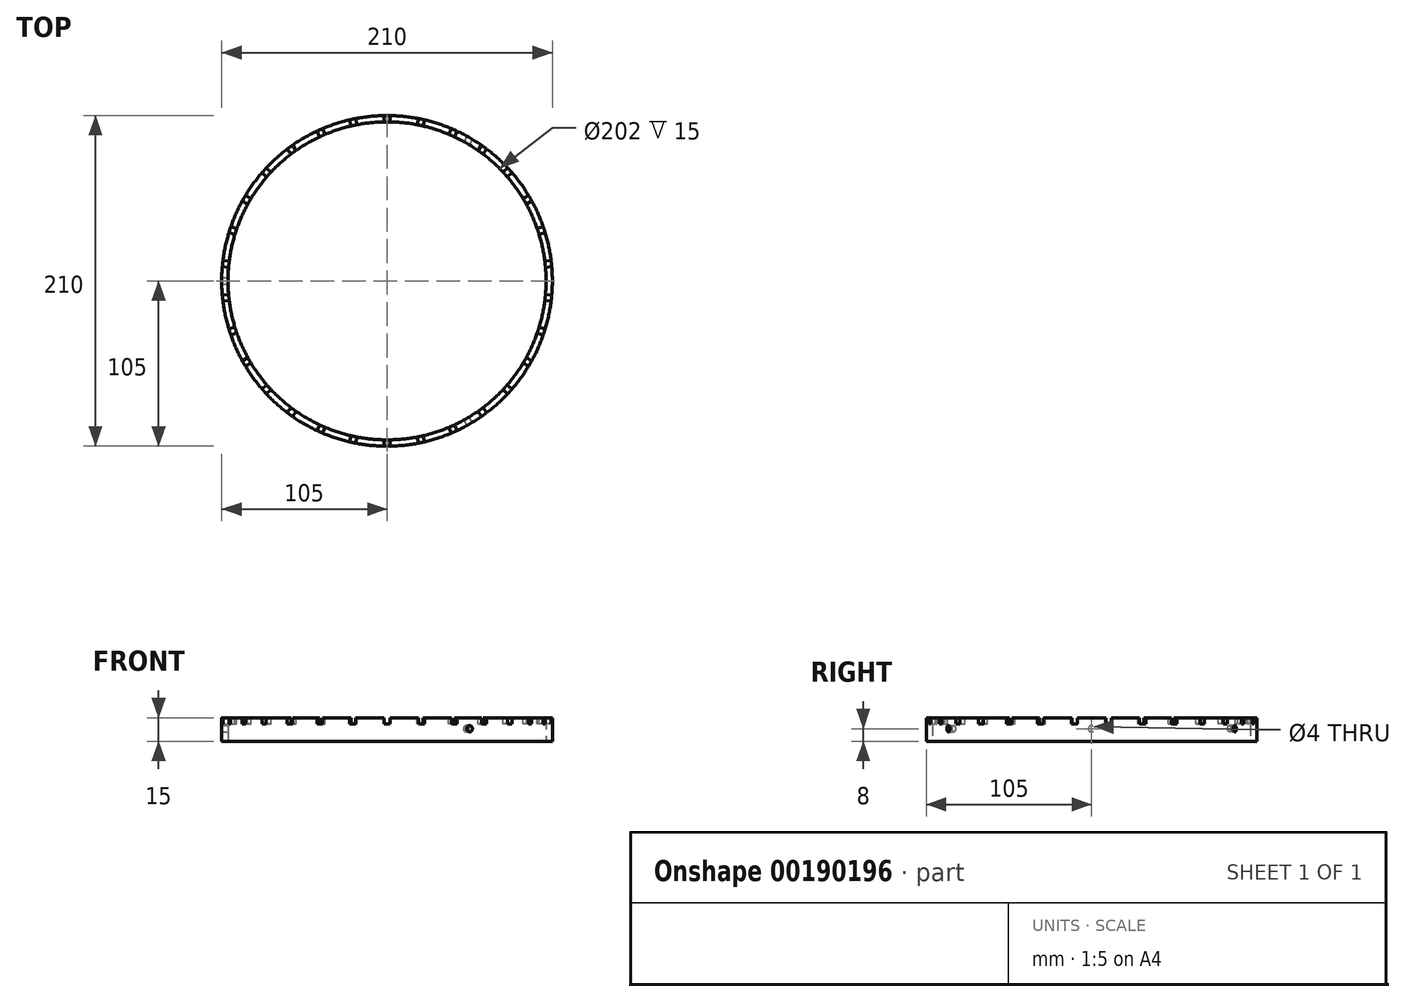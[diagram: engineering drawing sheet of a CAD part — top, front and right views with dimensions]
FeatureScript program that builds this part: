
annotation { "Feature Type Name" : "Feature", "Feature Type Description" : "" }
export const myFeature = defineFeature(function(context is Context, id is Id, definition is map)
    precondition{}
    {
        {
            var Q0;
            Q0=qCreatedBy(makeId("Top.planeOp"),FACE);
            var sketch = newSketch(context, id + "F0", { "sketchPlane" : qUnion([Q0])});
            skCircle(sketch, "E0", {"center": v(0, 0) * mm, "radius": 105 * mm});
            skCircle(sketch, "E1", {"center": v(0, 0) * mm, "radius": 101 * mm});
            skSolve(sketch);
        }
        {
            var Q0;
            Q0=makeQuery(id+"F0.imprint","IMPRINT",FACE,{"disambiguationData":[TD([[makeQuery(id+"F0.imprint","IMPRINT",EDGE,{"derivedFrom":sQuery(id+"F0.wireOp",EDGE,"E0")}),1.0]])]});
            extrude(context, id + "F1", {"entities" : qUnion([Q0]), "depth" : 15 * mm});
        }
        {
            var Q0;
            Q0=makeQuery(id+"F1.opExtrude","CAP_FACE",FACE,{"disambiguationData":[OSD([sQuery(id+"F0.wireOp",EDGE,"E0"),sQuery(id+"F0.wireOp",EDGE,"E1")])],"isStart":false});
            var sketch = newSketch(context, id + "F2", { "sketchPlane" : qUnion([Q0])});
            skLineSegment(sketch, "E2.bottom", {"start": v(2, 107.5) * mm, "end": v(-2, 107.5) * mm});
            skLineSegment(sketch, "E2.top", {"start": v(2, 97.86) * mm, "end": v(-2, 97.86) * mm});
            skLineSegment(sketch, "E2.left", {"start": v(2, 107.5) * mm, "end": v(2, 97.86) * mm});
            skLineSegment(sketch, "E2.right", {"start": v(-2, 107.5) * mm, "end": v(-2, 97.86) * mm});
            skPoint(sketch, "E2.middle", {"position": v(0, 102.68) * mm});
            skSolve(sketch);
        }
        {
            var Q0;
            {var subQ0=sQuery(id+"F2.wireOp",EDGE,"E2.left");var subQ1=makeQuery(id+"F1.opExtrude","CAP_EDGE",EDGE,{"disambiguationData":[OSD([sQuery(id+"F0.wireOp",EDGE,"E0")])],"isStart":false});var subQ2=makeQuery(id+"F2.imprint","INTERSECT",VERTEX,{"derivedFrom":[subQ1,subQ0]});Q0=makeQuery(id+"F2.imprint","IMPRINT",FACE,{"disambiguationData":[TD([[makeQuery(id+"F2.imprint","IMPRINT",EDGE,{"disambiguationData":[TD([[subQ2,-1.0]])],"derivedFrom":subQ0}),-1.0]])]});}
            extrude(context, id + "F3", {"entities" : qUnion([Q0]), "oppositeDirection" : true, "depth" : 4 * mm});
        }
        {
            var Q0;
            Q0=qCreatedBy(makeId("Right.planeOp"),FACE);
            var sketch = newSketch(context, id + "F4", { "sketchPlane" : qUnion([Q0])});
            skLineSegment(sketch, "E3", {"start": v(0, 0) * mm, "end": v(0, 34.11) * mm});
            skSolve(sketch);
        }
        {
            var Q0;
            Q0=makeQuery(id+"F3.opExtrude","SWEPT_BODY",BODY,{"disambiguationData":[OSD([sQuery(id+"F0.wireOp",EDGE,"E0"),sQuery(id+"F0.wireOp",EDGE,"E1"),sQuery(id+"F2.wireOp",EDGE,"E2.left"),sQuery(id+"F2.wireOp",EDGE,"E2.right")])]});
            var Q1;
            Q1=sQuery(id+"F4.wireOp",EDGE,"E3");
            circularPattern(context, id + "F5", {"entities" : qUnion([Q0]), "axis" : qUnion([Q1]), "angle" : 360 * degree, "instanceCount" : 30, "equalSpace" : true});
        }
        {
            var Q0;
            Q0=qCreatedBy(makeId("Right.planeOp"),FACE);
            var sketch = newSketch(context, id + "F6", { "sketchPlane" : qUnion([Q0])});
            skCircle(sketch, "E4", {"center": v(0, 8) * mm, "radius": 2 * mm});
            skSolve(sketch);
        }
        {
            var Q0;
            Q0=makeQuery(id+"F6.imprint","IMPRINT",FACE,{"disambiguationData":[TD([[makeQuery(id+"F6.imprint","IMPRINT",EDGE,{"derivedFrom":sQuery(id+"F6.wireOp",EDGE,"E4")}),1.0]])]});
            extrude(context, id + "F7", {"entities" : qUnion([Q0]), "oppositeDirection" : true, "depth" : 120.9 * mm, "hasSecondDirection" : true, "secondDirectionOppositeDirection" : true, "secondDirectionDepth" : 84.3 * mm});
        }
        {
            var Q0;
            Q0=makeQuery(id+"F7.opExtrude","SWEPT_BODY",BODY,{"disambiguationData":[OSD([sQuery(id+"F6.wireOp",EDGE,"E4")])]});
            var Q1;
            Q1=sQuery(id+"F4.wireOp",EDGE,"E3");
            circularPattern(context, id + "F8", {"entities" : qUnion([Q0]), "axis" : qUnion([Q1]), "angle" : 360 * degree, "instanceCount" : 3, "equalSpace" : true});
        }
        {
            var Q0;
            Q0=makeQuery(id+"F5.opPattern","COPY",BODY,{"derivedFrom":makeQuery(id+"F3.opExtrude","SWEPT_BODY",BODY,{"disambiguationData":[OSD([sQuery(id+"F0.wireOp",EDGE,"E0"),sQuery(id+"F0.wireOp",EDGE,"E1"),sQuery(id+"F2.wireOp",EDGE,"E2.left"),sQuery(id+"F2.wireOp",EDGE,"E2.right")])]}),"instanceName":"23"});
            var Q1;
            Q1=makeQuery(id+"F3.opExtrude","SWEPT_BODY",BODY,{"disambiguationData":[OSD([sQuery(id+"F0.wireOp",EDGE,"E0"),sQuery(id+"F0.wireOp",EDGE,"E1"),sQuery(id+"F2.wireOp",EDGE,"E2.left"),sQuery(id+"F2.wireOp",EDGE,"E2.right")])]});
            var Q2;
            Q2=makeQuery(id+"F5.opPattern","COPY",BODY,{"derivedFrom":makeQuery(id+"F3.opExtrude","SWEPT_BODY",BODY,{"disambiguationData":[OSD([sQuery(id+"F0.wireOp",EDGE,"E0"),sQuery(id+"F0.wireOp",EDGE,"E1"),sQuery(id+"F2.wireOp",EDGE,"E2.left"),sQuery(id+"F2.wireOp",EDGE,"E2.right")])]}),"instanceName":"1"});
            var Q3;
            Q3=makeQuery(id+"F5.opPattern","COPY",BODY,{"derivedFrom":makeQuery(id+"F3.opExtrude","SWEPT_BODY",BODY,{"disambiguationData":[OSD([sQuery(id+"F0.wireOp",EDGE,"E0"),sQuery(id+"F0.wireOp",EDGE,"E1"),sQuery(id+"F2.wireOp",EDGE,"E2.left"),sQuery(id+"F2.wireOp",EDGE,"E2.right")])]}),"instanceName":"2"});
            var Q4;
            Q4=makeQuery(id+"F5.opPattern","COPY",BODY,{"derivedFrom":makeQuery(id+"F3.opExtrude","SWEPT_BODY",BODY,{"disambiguationData":[OSD([sQuery(id+"F0.wireOp",EDGE,"E0"),sQuery(id+"F0.wireOp",EDGE,"E1"),sQuery(id+"F2.wireOp",EDGE,"E2.left"),sQuery(id+"F2.wireOp",EDGE,"E2.right")])]}),"instanceName":"3"});
            var Q5;
            Q5=makeQuery(id+"F5.opPattern","COPY",BODY,{"derivedFrom":makeQuery(id+"F3.opExtrude","SWEPT_BODY",BODY,{"disambiguationData":[OSD([sQuery(id+"F0.wireOp",EDGE,"E0"),sQuery(id+"F0.wireOp",EDGE,"E1"),sQuery(id+"F2.wireOp",EDGE,"E2.left"),sQuery(id+"F2.wireOp",EDGE,"E2.right")])]}),"instanceName":"4"});
            var Q6;
            Q6=makeQuery(id+"F5.opPattern","COPY",BODY,{"derivedFrom":makeQuery(id+"F3.opExtrude","SWEPT_BODY",BODY,{"disambiguationData":[OSD([sQuery(id+"F0.wireOp",EDGE,"E0"),sQuery(id+"F0.wireOp",EDGE,"E1"),sQuery(id+"F2.wireOp",EDGE,"E2.left"),sQuery(id+"F2.wireOp",EDGE,"E2.right")])]}),"instanceName":"5"});
            var Q7;
            Q7=makeQuery(id+"F5.opPattern","COPY",BODY,{"derivedFrom":makeQuery(id+"F3.opExtrude","SWEPT_BODY",BODY,{"disambiguationData":[OSD([sQuery(id+"F0.wireOp",EDGE,"E0"),sQuery(id+"F0.wireOp",EDGE,"E1"),sQuery(id+"F2.wireOp",EDGE,"E2.left"),sQuery(id+"F2.wireOp",EDGE,"E2.right")])]}),"instanceName":"6"});
            var Q8;
            Q8=makeQuery(id+"F5.opPattern","COPY",BODY,{"derivedFrom":makeQuery(id+"F3.opExtrude","SWEPT_BODY",BODY,{"disambiguationData":[OSD([sQuery(id+"F0.wireOp",EDGE,"E0"),sQuery(id+"F0.wireOp",EDGE,"E1"),sQuery(id+"F2.wireOp",EDGE,"E2.left"),sQuery(id+"F2.wireOp",EDGE,"E2.right")])]}),"instanceName":"7"});
            var Q9;
            Q9=makeQuery(id+"F5.opPattern","COPY",BODY,{"derivedFrom":makeQuery(id+"F3.opExtrude","SWEPT_BODY",BODY,{"disambiguationData":[OSD([sQuery(id+"F0.wireOp",EDGE,"E0"),sQuery(id+"F0.wireOp",EDGE,"E1"),sQuery(id+"F2.wireOp",EDGE,"E2.left"),sQuery(id+"F2.wireOp",EDGE,"E2.right")])]}),"instanceName":"8"});
            var Q10;
            Q10=makeQuery(id+"F5.opPattern","COPY",BODY,{"derivedFrom":makeQuery(id+"F3.opExtrude","SWEPT_BODY",BODY,{"disambiguationData":[OSD([sQuery(id+"F0.wireOp",EDGE,"E0"),sQuery(id+"F0.wireOp",EDGE,"E1"),sQuery(id+"F2.wireOp",EDGE,"E2.left"),sQuery(id+"F2.wireOp",EDGE,"E2.right")])]}),"instanceName":"9"});
            var Q11;
            Q11=makeQuery(id+"F5.opPattern","COPY",BODY,{"derivedFrom":makeQuery(id+"F3.opExtrude","SWEPT_BODY",BODY,{"disambiguationData":[OSD([sQuery(id+"F0.wireOp",EDGE,"E0"),sQuery(id+"F0.wireOp",EDGE,"E1"),sQuery(id+"F2.wireOp",EDGE,"E2.left"),sQuery(id+"F2.wireOp",EDGE,"E2.right")])]}),"instanceName":"10"});
            var Q12;
            Q12=makeQuery(id+"F5.opPattern","COPY",BODY,{"derivedFrom":makeQuery(id+"F3.opExtrude","SWEPT_BODY",BODY,{"disambiguationData":[OSD([sQuery(id+"F0.wireOp",EDGE,"E0"),sQuery(id+"F0.wireOp",EDGE,"E1"),sQuery(id+"F2.wireOp",EDGE,"E2.left"),sQuery(id+"F2.wireOp",EDGE,"E2.right")])]}),"instanceName":"11"});
            var Q13;
            Q13=makeQuery(id+"F5.opPattern","COPY",BODY,{"derivedFrom":makeQuery(id+"F3.opExtrude","SWEPT_BODY",BODY,{"disambiguationData":[OSD([sQuery(id+"F0.wireOp",EDGE,"E0"),sQuery(id+"F0.wireOp",EDGE,"E1"),sQuery(id+"F2.wireOp",EDGE,"E2.left"),sQuery(id+"F2.wireOp",EDGE,"E2.right")])]}),"instanceName":"12"});
            var Q14;
            Q14=makeQuery(id+"F5.opPattern","COPY",BODY,{"derivedFrom":makeQuery(id+"F3.opExtrude","SWEPT_BODY",BODY,{"disambiguationData":[OSD([sQuery(id+"F0.wireOp",EDGE,"E0"),sQuery(id+"F0.wireOp",EDGE,"E1"),sQuery(id+"F2.wireOp",EDGE,"E2.left"),sQuery(id+"F2.wireOp",EDGE,"E2.right")])]}),"instanceName":"13"});
            var Q15;
            Q15=makeQuery(id+"F5.opPattern","COPY",BODY,{"derivedFrom":makeQuery(id+"F3.opExtrude","SWEPT_BODY",BODY,{"disambiguationData":[OSD([sQuery(id+"F0.wireOp",EDGE,"E0"),sQuery(id+"F0.wireOp",EDGE,"E1"),sQuery(id+"F2.wireOp",EDGE,"E2.left"),sQuery(id+"F2.wireOp",EDGE,"E2.right")])]}),"instanceName":"14"});
            var Q16;
            Q16=makeQuery(id+"F5.opPattern","COPY",BODY,{"derivedFrom":makeQuery(id+"F3.opExtrude","SWEPT_BODY",BODY,{"disambiguationData":[OSD([sQuery(id+"F0.wireOp",EDGE,"E0"),sQuery(id+"F0.wireOp",EDGE,"E1"),sQuery(id+"F2.wireOp",EDGE,"E2.left"),sQuery(id+"F2.wireOp",EDGE,"E2.right")])]}),"instanceName":"15"});
            var Q17;
            Q17=makeQuery(id+"F5.opPattern","COPY",BODY,{"derivedFrom":makeQuery(id+"F3.opExtrude","SWEPT_BODY",BODY,{"disambiguationData":[OSD([sQuery(id+"F0.wireOp",EDGE,"E0"),sQuery(id+"F0.wireOp",EDGE,"E1"),sQuery(id+"F2.wireOp",EDGE,"E2.left"),sQuery(id+"F2.wireOp",EDGE,"E2.right")])]}),"instanceName":"16"});
            var Q18;
            Q18=makeQuery(id+"F5.opPattern","COPY",BODY,{"derivedFrom":makeQuery(id+"F3.opExtrude","SWEPT_BODY",BODY,{"disambiguationData":[OSD([sQuery(id+"F0.wireOp",EDGE,"E0"),sQuery(id+"F0.wireOp",EDGE,"E1"),sQuery(id+"F2.wireOp",EDGE,"E2.left"),sQuery(id+"F2.wireOp",EDGE,"E2.right")])]}),"instanceName":"17"});
            var Q19;
            Q19=makeQuery(id+"F5.opPattern","COPY",BODY,{"derivedFrom":makeQuery(id+"F3.opExtrude","SWEPT_BODY",BODY,{"disambiguationData":[OSD([sQuery(id+"F0.wireOp",EDGE,"E0"),sQuery(id+"F0.wireOp",EDGE,"E1"),sQuery(id+"F2.wireOp",EDGE,"E2.left"),sQuery(id+"F2.wireOp",EDGE,"E2.right")])]}),"instanceName":"18"});
            var Q20;
            Q20=makeQuery(id+"F5.opPattern","COPY",BODY,{"derivedFrom":makeQuery(id+"F3.opExtrude","SWEPT_BODY",BODY,{"disambiguationData":[OSD([sQuery(id+"F0.wireOp",EDGE,"E0"),sQuery(id+"F0.wireOp",EDGE,"E1"),sQuery(id+"F2.wireOp",EDGE,"E2.left"),sQuery(id+"F2.wireOp",EDGE,"E2.right")])]}),"instanceName":"19"});
            var Q21;
            Q21=makeQuery(id+"F5.opPattern","COPY",BODY,{"derivedFrom":makeQuery(id+"F3.opExtrude","SWEPT_BODY",BODY,{"disambiguationData":[OSD([sQuery(id+"F0.wireOp",EDGE,"E0"),sQuery(id+"F0.wireOp",EDGE,"E1"),sQuery(id+"F2.wireOp",EDGE,"E2.left"),sQuery(id+"F2.wireOp",EDGE,"E2.right")])]}),"instanceName":"20"});
            var Q22;
            Q22=makeQuery(id+"F5.opPattern","COPY",BODY,{"derivedFrom":makeQuery(id+"F3.opExtrude","SWEPT_BODY",BODY,{"disambiguationData":[OSD([sQuery(id+"F0.wireOp",EDGE,"E0"),sQuery(id+"F0.wireOp",EDGE,"E1"),sQuery(id+"F2.wireOp",EDGE,"E2.left"),sQuery(id+"F2.wireOp",EDGE,"E2.right")])]}),"instanceName":"21"});
            var Q23;
            Q23=makeQuery(id+"F5.opPattern","COPY",BODY,{"derivedFrom":makeQuery(id+"F3.opExtrude","SWEPT_BODY",BODY,{"disambiguationData":[OSD([sQuery(id+"F0.wireOp",EDGE,"E0"),sQuery(id+"F0.wireOp",EDGE,"E1"),sQuery(id+"F2.wireOp",EDGE,"E2.left"),sQuery(id+"F2.wireOp",EDGE,"E2.right")])]}),"instanceName":"22"});
            var Q24;
            Q24=makeQuery(id+"F5.opPattern","COPY",BODY,{"derivedFrom":makeQuery(id+"F3.opExtrude","SWEPT_BODY",BODY,{"disambiguationData":[OSD([sQuery(id+"F0.wireOp",EDGE,"E0"),sQuery(id+"F0.wireOp",EDGE,"E1"),sQuery(id+"F2.wireOp",EDGE,"E2.left"),sQuery(id+"F2.wireOp",EDGE,"E2.right")])]}),"instanceName":"29"});
            var Q25;
            Q25=makeQuery(id+"F5.opPattern","COPY",BODY,{"derivedFrom":makeQuery(id+"F3.opExtrude","SWEPT_BODY",BODY,{"disambiguationData":[OSD([sQuery(id+"F0.wireOp",EDGE,"E0"),sQuery(id+"F0.wireOp",EDGE,"E1"),sQuery(id+"F2.wireOp",EDGE,"E2.left"),sQuery(id+"F2.wireOp",EDGE,"E2.right")])]}),"instanceName":"27"});
            var Q26;
            Q26=makeQuery(id+"F5.opPattern","COPY",BODY,{"derivedFrom":makeQuery(id+"F3.opExtrude","SWEPT_BODY",BODY,{"disambiguationData":[OSD([sQuery(id+"F0.wireOp",EDGE,"E0"),sQuery(id+"F0.wireOp",EDGE,"E1"),sQuery(id+"F2.wireOp",EDGE,"E2.left"),sQuery(id+"F2.wireOp",EDGE,"E2.right")])]}),"instanceName":"26"});
            var Q27;
            Q27=makeQuery(id+"F5.opPattern","COPY",BODY,{"derivedFrom":makeQuery(id+"F3.opExtrude","SWEPT_BODY",BODY,{"disambiguationData":[OSD([sQuery(id+"F0.wireOp",EDGE,"E0"),sQuery(id+"F0.wireOp",EDGE,"E1"),sQuery(id+"F2.wireOp",EDGE,"E2.left"),sQuery(id+"F2.wireOp",EDGE,"E2.right")])]}),"instanceName":"25"});
            var Q28;
            Q28=makeQuery(id+"F5.opPattern","COPY",BODY,{"derivedFrom":makeQuery(id+"F3.opExtrude","SWEPT_BODY",BODY,{"disambiguationData":[OSD([sQuery(id+"F0.wireOp",EDGE,"E0"),sQuery(id+"F0.wireOp",EDGE,"E1"),sQuery(id+"F2.wireOp",EDGE,"E2.left"),sQuery(id+"F2.wireOp",EDGE,"E2.right")])]}),"instanceName":"28"});
            var Q29;
            Q29=makeQuery(id+"F5.opPattern","COPY",BODY,{"derivedFrom":makeQuery(id+"F3.opExtrude","SWEPT_BODY",BODY,{"disambiguationData":[OSD([sQuery(id+"F0.wireOp",EDGE,"E0"),sQuery(id+"F0.wireOp",EDGE,"E1"),sQuery(id+"F2.wireOp",EDGE,"E2.left"),sQuery(id+"F2.wireOp",EDGE,"E2.right")])]}),"instanceName":"24"});
            var Q30;
            Q30=makeQuery(id+"F8.opPattern","COPY",BODY,{"derivedFrom":makeQuery(id+"F7.opExtrude","SWEPT_BODY",BODY,{"disambiguationData":[OSD([sQuery(id+"F6.wireOp",EDGE,"E4")])]}),"instanceName":"2"});
            var Q31;
            Q31=makeQuery(id+"F8.opPattern","COPY",BODY,{"derivedFrom":makeQuery(id+"F7.opExtrude","SWEPT_BODY",BODY,{"disambiguationData":[OSD([sQuery(id+"F6.wireOp",EDGE,"E4")])]}),"instanceName":"1"});
            var Q32;
            Q32=makeQuery(id+"F7.opExtrude","SWEPT_BODY",BODY,{"disambiguationData":[OSD([sQuery(id+"F6.wireOp",EDGE,"E4")])]});
            var Q33;
            Q33=makeQuery(id+"F1.opExtrude","SWEPT_BODY",BODY,{"disambiguationData":[OSD([sQuery(id+"F0.wireOp",EDGE,"E0"),sQuery(id+"F0.wireOp",EDGE,"E1")])]});
            booleanBodies(context, id + "F9", {"operationType" : BooleanOperationType.SUBTRACTION, "tools" : qUnion([Q0, Q1, Q2, Q3, Q4, Q5, Q6, Q7, Q8, Q9, Q10, Q11, Q12, Q13, Q14, Q15, Q16, Q17, Q18, Q19, Q20, Q21, Q22, Q23, Q24, Q25, Q26, Q27, Q28, Q29, Q30, Q31, Q32]), "targets" : qUnion([Q33])});
        }
    });
